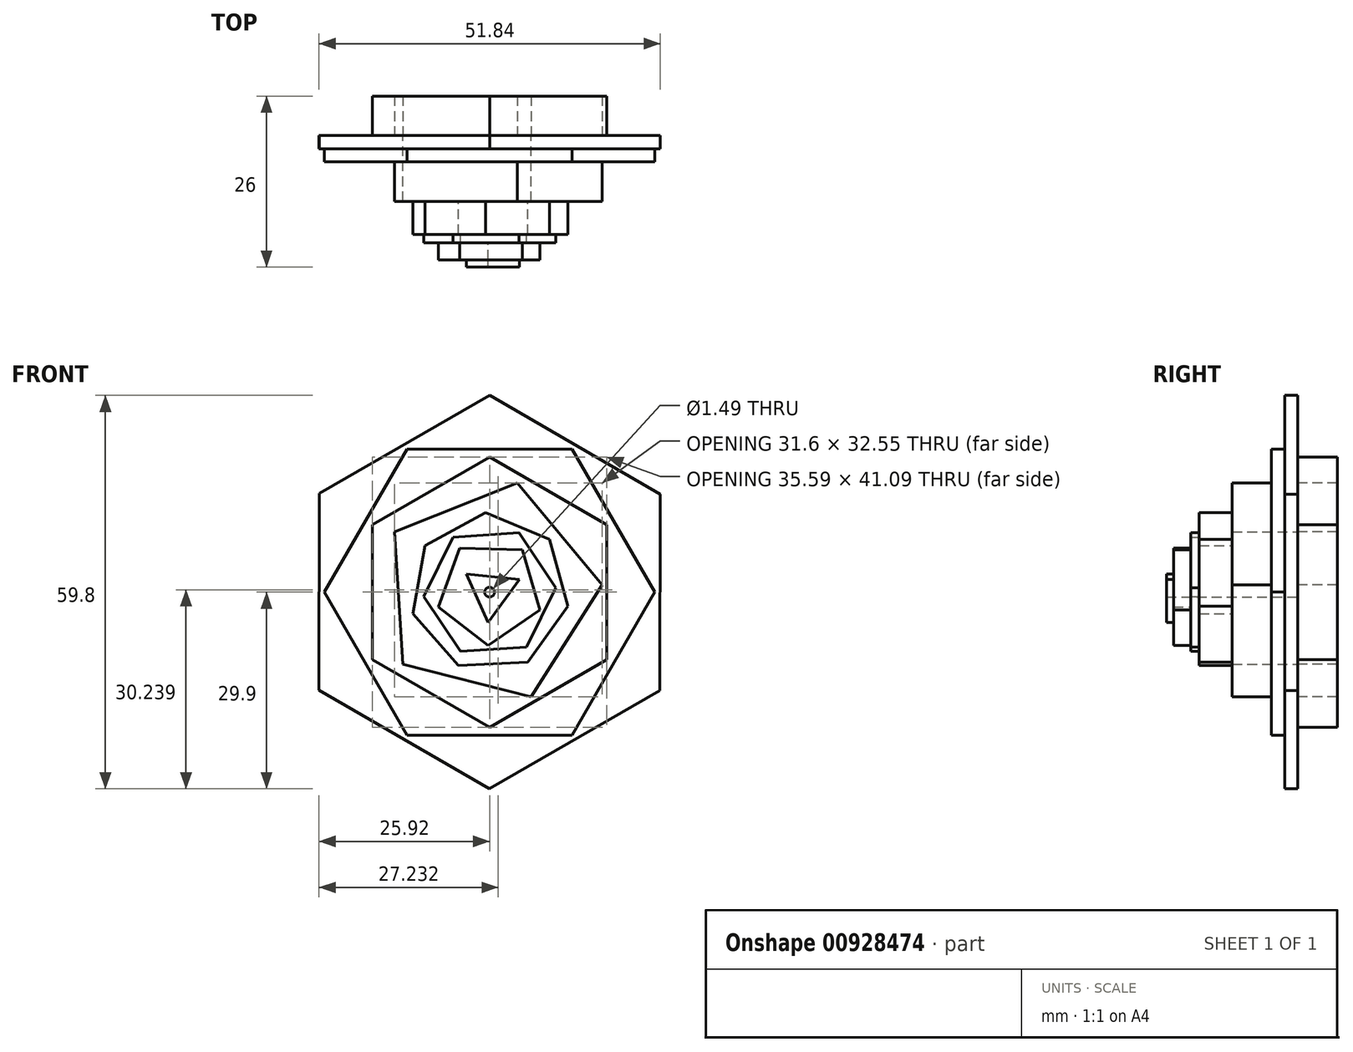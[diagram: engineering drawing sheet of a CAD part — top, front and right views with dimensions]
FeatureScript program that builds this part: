
annotation { "Feature Type Name" : "Feature", "Feature Type Description" : "" }
export const myFeature = defineFeature(function(context is Context, id is Id, definition is map)
    precondition{}
    {
        {
            var Q0;
            Q0=qCreatedBy(makeId("Front.planeOp"),FACE);
            var sketch = newSketch(context, id + "F0", { "sketchPlane" : qUnion([Q0])});
            skCircle(sketch, "E0.cCircle", {"center": v(0, 0) * mm, "radius": 25.9 * mm, "construction": true});
            skLineSegment(sketch, "E0.0", {"start": v(25.87, -15) * mm, "end": v(-0.05, -29.9) * mm});
            skLineSegment(sketch, "E0.1", {"start": v(-0.05, -29.9) * mm, "end": v(-25.92, -14.9) * mm});
            skLineSegment(sketch, "E0.2", {"start": v(-25.92, -14.9) * mm, "end": v(-25.87, 15) * mm});
            skLineSegment(sketch, "E0.3", {"start": v(-25.87, 15) * mm, "end": v(0.05, 29.9) * mm});
            skLineSegment(sketch, "E0.4", {"start": v(0.05, 29.9) * mm, "end": v(25.92, 14.9) * mm});
            skLineSegment(sketch, "E0.5", {"start": v(25.92, 14.9) * mm, "end": v(25.87, -15) * mm});
            skPoint(sketch, "E0.0.midPoint", {"position": v(12.9, -22.44) * mm});
            skCircle(sketch, "E1.cCircle", {"center": v(0, 0) * mm, "radius": 21.75 * mm, "construction": true});
            skLineSegment(sketch, "E1.0", {"start": v(12.56, -21.75) * mm, "end": v(-12.56, -21.75) * mm});
            skLineSegment(sketch, "E1.1", {"start": v(-12.56, -21.75) * mm, "end": v(-25.11, 0) * mm});
            skLineSegment(sketch, "E1.2", {"start": v(-25.11, 0) * mm, "end": v(-12.56, 21.75) * mm});
            skLineSegment(sketch, "E1.3", {"start": v(-12.56, 21.75) * mm, "end": v(12.56, 21.75) * mm});
            skLineSegment(sketch, "E1.4", {"start": v(12.56, 21.75) * mm, "end": v(25.11, 0) * mm});
            skLineSegment(sketch, "E1.5", {"start": v(25.11, 0) * mm, "end": v(12.56, -21.75) * mm});
            skPoint(sketch, "E1.0.midPoint", {"position": v(0, -21.75) * mm});
            skCircle(sketch, "E2.cCircle", {"center": v(0, 0) * mm, "radius": 17.8 * mm, "construction": true});
            skLineSegment(sketch, "E2.0", {"start": v(17.8, 10.27) * mm, "end": v(17.8, -10.27) * mm});
            skLineSegment(sketch, "E2.1", {"start": v(17.8, -10.27) * mm, "end": v(0, -20.55) * mm});
            skLineSegment(sketch, "E2.2", {"start": v(0, -20.55) * mm, "end": v(-17.8, -10.27) * mm});
            skLineSegment(sketch, "E2.3", {"start": v(-17.8, -10.27) * mm, "end": v(-17.8, 10.27) * mm});
            skLineSegment(sketch, "E2.4", {"start": v(-17.8, 10.27) * mm, "end": v(0, 20.55) * mm});
            skLineSegment(sketch, "E2.5", {"start": v(0, 20.55) * mm, "end": v(17.8, 10.27) * mm});
            skPoint(sketch, "E2.0.midPoint", {"position": v(17.8, 0) * mm});
            skCircle(sketch, "E3.cCircle", {"center": v(0, 0) * mm, "radius": 13.87 * mm, "construction": true});
            skLineSegment(sketch, "E3.0", {"start": v(17.11, 1.1) * mm, "end": v(6.33, -15.93) * mm});
            skLineSegment(sketch, "E3.1", {"start": v(6.33, -15.93) * mm, "end": v(-13.2, -10.94) * mm});
            skLineSegment(sketch, "E3.2", {"start": v(-13.2, -10.94) * mm, "end": v(-14.49, 9.17) * mm});
            skLineSegment(sketch, "E3.3", {"start": v(-14.49, 9.17) * mm, "end": v(4.24, 16.61) * mm});
            skLineSegment(sketch, "E3.4", {"start": v(4.24, 16.61) * mm, "end": v(17.11, 1.1) * mm});
            skPoint(sketch, "E3.0.midPoint", {"position": v(11.72, -7.42) * mm});
            skCircle(sketch, "E4.cCircle", {"center": v(0, 0) * mm, "radius": 10.91 * mm, "construction": true});
            skLineSegment(sketch, "E4.0", {"start": v(11.93, -2.11) * mm, "end": v(5.79, -10.64) * mm});
            skLineSegment(sketch, "E4.1", {"start": v(5.79, -10.64) * mm, "end": v(-4.71, -11.16) * mm});
            skLineSegment(sketch, "E4.2", {"start": v(-4.71, -11.16) * mm, "end": v(-11.66, -3.27) * mm});
            skLineSegment(sketch, "E4.3", {"start": v(-11.66, -3.27) * mm, "end": v(-9.83, 7.08) * mm});
            skLineSegment(sketch, "E4.4", {"start": v(-9.83, 7.08) * mm, "end": v(-0.6, 12.1) * mm});
            skLineSegment(sketch, "E4.5", {"start": v(-0.6, 12.1) * mm, "end": v(9.09, 8) * mm});
            skLineSegment(sketch, "E4.6", {"start": v(9.09, 8) * mm, "end": v(11.93, -2.11) * mm});
            skPoint(sketch, "E4.0.midPoint", {"position": v(8.86, -6.37) * mm});
            skCircle(sketch, "E5.cCircle", {"center": v(0, 0) * mm, "radius": 8.7 * mm, "construction": true});
            skLineSegment(sketch, "E5.0", {"start": v(10.03, 0.65) * mm, "end": v(5.58, -8.36) * mm});
            skLineSegment(sketch, "E5.1", {"start": v(5.58, -8.36) * mm, "end": v(-4.45, -9.01) * mm});
            skLineSegment(sketch, "E5.2", {"start": v(-4.45, -9.01) * mm, "end": v(-10.03, -0.65) * mm});
            skLineSegment(sketch, "E5.3", {"start": v(-10.03, -0.65) * mm, "end": v(-5.58, 8.36) * mm});
            skLineSegment(sketch, "E5.4", {"start": v(-5.58, 8.36) * mm, "end": v(4.45, 9.01) * mm});
            skLineSegment(sketch, "E5.5", {"start": v(4.45, 9.01) * mm, "end": v(10.03, 0.65) * mm});
            skPoint(sketch, "E5.0.midPoint", {"position": v(7.8, -3.85) * mm});
            skCircle(sketch, "E6.cCircle", {"center": v(0, 0) * mm, "radius": 6.57 * mm, "construction": true});
            skLineSegment(sketch, "E6.0", {"start": v(7.65, -2.74) * mm, "end": v(-0.24, -8.12) * mm});
            skLineSegment(sketch, "E6.1", {"start": v(-0.24, -8.12) * mm, "end": v(-7.8, -2.28) * mm});
            skLineSegment(sketch, "E6.2", {"start": v(-7.8, -2.28) * mm, "end": v(-4.58, 6.71) * mm});
            skLineSegment(sketch, "E6.3", {"start": v(-4.58, 6.71) * mm, "end": v(4.97, 6.43) * mm});
            skLineSegment(sketch, "E6.4", {"start": v(4.97, 6.43) * mm, "end": v(7.65, -2.74) * mm});
            skPoint(sketch, "E6.0.midPoint", {"position": v(3.7, -5.43) * mm});
            skCircle(sketch, "E7.cCircle", {"center": v(0.24, 0.03) * mm, "radius": 2.33 * mm, "construction": true});
            skLineSegment(sketch, "E7.0", {"start": v(4.5, 1.94) * mm, "end": v(-0.23, -4.6) * mm});
            skLineSegment(sketch, "E7.1", {"start": v(-0.23, -4.6) * mm, "end": v(-3.54, 2.77) * mm});
            skLineSegment(sketch, "E7.2", {"start": v(-3.54, 2.77) * mm, "end": v(4.5, 1.94) * mm});
            skPoint(sketch, "E7.0.midPoint", {"position": v(2.13, -1.33) * mm});
            skCircle(sketch, "E8", {"center": v(0, 0) * mm, "radius": 0.74 * mm});
            skSolve(sketch);
        }
        {
            var Q0;
            Q0=makeQuery(id+"F0.imprint","IMPRINT",FACE,{"disambiguationData":[TD([[makeQuery(id+"F0.imprint","IMPRINT",EDGE,{"derivedFrom":sQuery(id+"F0.wireOp",EDGE,"E1.0")}),-1.0]])]});
            extrude(context, id + "F1", {"entities" : qUnion([Q0]), "depth" : 4 * mm, "offsetDistance" : 25.4 * mm});
        }
        {
            var Q0;
            Q0=makeQuery(id+"F0.imprint","IMPRINT",FACE,{"disambiguationData":[TD([[makeQuery(id+"F0.imprint","IMPRINT",EDGE,{"derivedFrom":sQuery(id+"F0.wireOp",EDGE,"E0.0")}),-1.0]])]});
            extrude(context, id + "F2", {"entities" : qUnion([Q0]), "operationType" : NewBodyOperationType.ADD, "depth" : 2 * mm, "offsetDistance" : 25 * mm});
        }
        {
            var Q0;
            Q0=makeQuery(id+"F0.imprint","IMPRINT",FACE,{"disambiguationData":[TD([[makeQuery(id+"F0.imprint","IMPRINT",EDGE,{"derivedFrom":sQuery(id+"F0.wireOp",EDGE,"E2.0")}),-1.0]])]});
            extrude(context, id + "F3", {"entities" : qUnion([Q0]), "operationType" : NewBodyOperationType.ADD, "oppositeDirection" : true, "depth" : 6 * mm, "offsetDistance" : 25 * mm});
        }
        {
            var Q0;
            Q0=makeQuery(id+"F0.imprint","IMPRINT",FACE,{"disambiguationData":[TD([[makeQuery(id+"F0.imprint","IMPRINT",EDGE,{"derivedFrom":sQuery(id+"F0.wireOp",EDGE,"E3.0")}),-1.0]])]});
            extrude(context, id + "F4", {"entities" : qUnion([Q0]), "depth" : 10 * mm, "offsetDistance" : 25 * mm});
        }
        {
            var Q0;
            Q0=makeQuery(id+"F0.imprint","IMPRINT",FACE,{"disambiguationData":[TD([[makeQuery(id+"F0.imprint","IMPRINT",EDGE,{"derivedFrom":sQuery(id+"F0.wireOp",EDGE,"E4.0")}),-1.0]])]});
            extrude(context, id + "F5", {"entities" : qUnion([Q0]), "operationType" : NewBodyOperationType.ADD, "depth" : 15 * mm, "offsetDistance" : 25 * mm});
        }
        {
            var Q0;
            Q0=makeQuery(id+"F0.imprint","IMPRINT",FACE,{"disambiguationData":[TD([[makeQuery(id+"F0.imprint","IMPRINT",EDGE,{"derivedFrom":sQuery(id+"F0.wireOp",EDGE,"E5.0")}),-1.0]])]});
            extrude(context, id + "F6", {"entities" : qUnion([Q0]), "operationType" : NewBodyOperationType.ADD, "depth" : 16.3 * mm, "offsetDistance" : 25 * mm});
        }
        {
            var Q0;
            Q0=makeQuery(id+"F0.imprint","IMPRINT",FACE,{"disambiguationData":[TD([[makeQuery(id+"F0.imprint","IMPRINT",EDGE,{"derivedFrom":sQuery(id+"F0.wireOp",EDGE,"E6.0")}),-1.0]])]});
            extrude(context, id + "F7", {"entities" : qUnion([Q0]), "operationType" : NewBodyOperationType.ADD, "depth" : 18.9 * mm, "offsetDistance" : 25 * mm});
        }
        {
            var Q0;
            Q0=makeQuery(id+"F0.imprint","IMPRINT",FACE,{"disambiguationData":[TD([[makeQuery(id+"F0.imprint","IMPRINT",EDGE,{"derivedFrom":sQuery(id+"F0.wireOp",EDGE,"E7.0")}),-1.0]])]});
            extrude(context, id + "F8", {"entities" : qUnion([Q0]), "operationType" : NewBodyOperationType.ADD, "depth" : 20 * mm, "offsetDistance" : 25 * mm});
        }
    });
